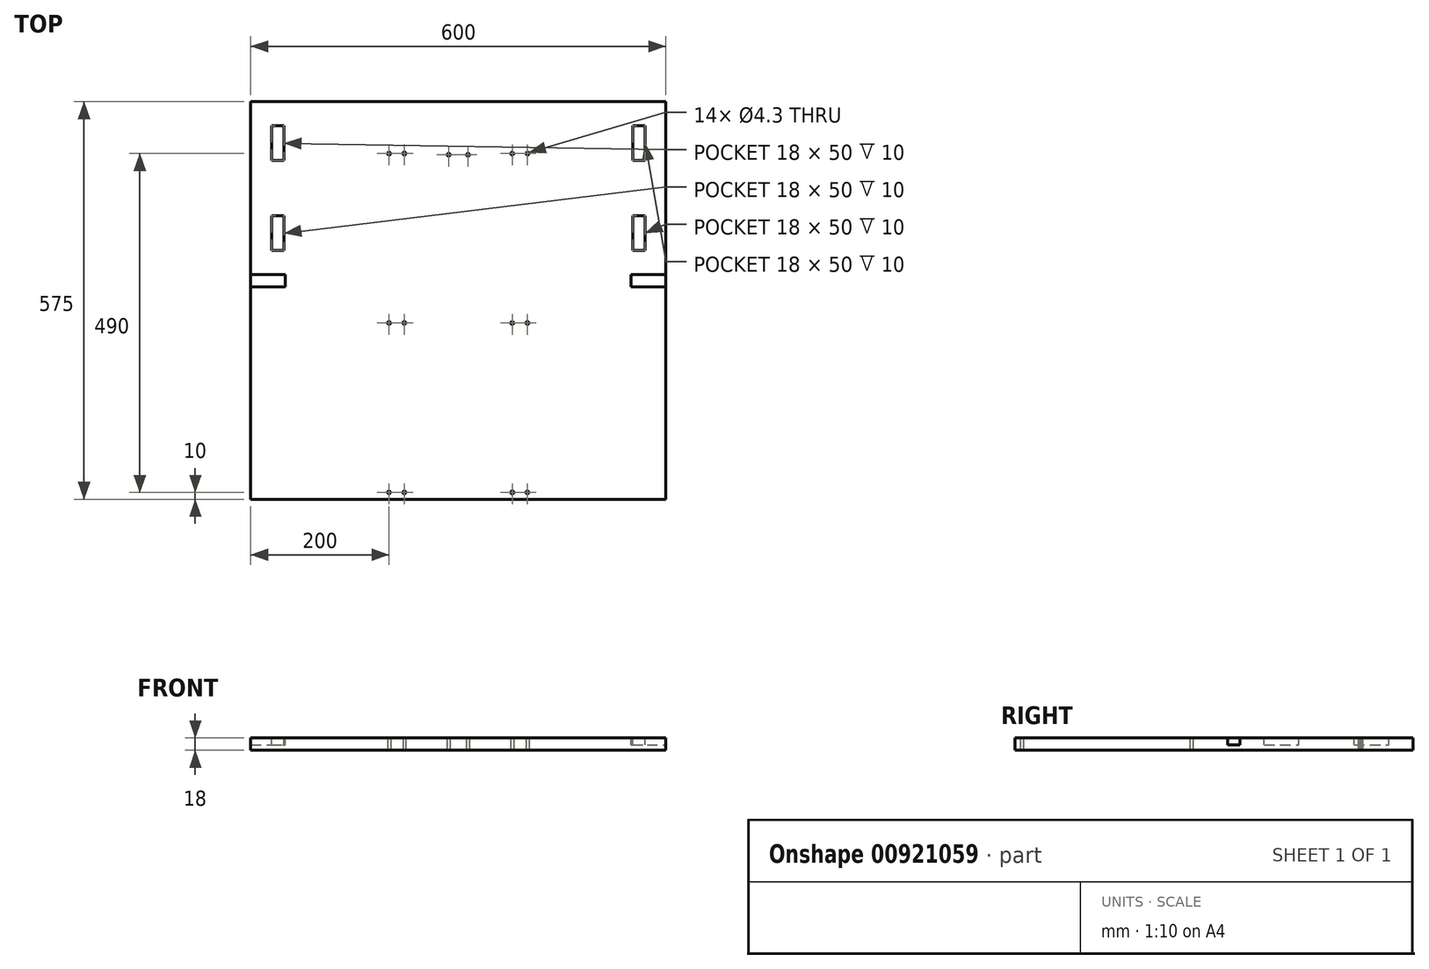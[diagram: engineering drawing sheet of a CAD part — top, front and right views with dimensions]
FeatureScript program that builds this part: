
annotation { "Feature Type Name" : "Feature", "Feature Type Description" : "" }
export const myFeature = defineFeature(function(context is Context, id is Id, definition is map)
    precondition{}
    {
        {
            var Q0;
            Q0=qCreatedBy(makeId("Top.planeOp"),FACE);
            var sketch = newSketch(context, id + "F0", { "sketchPlane" : qUnion([Q0])});
            skLineSegment(sketch, "E0.bottom", {"start": v(0, 0) * mm, "end": v(600, 0) * mm});
            skLineSegment(sketch, "E0.top", {"start": v(0, -575) * mm, "end": v(600, -575) * mm});
            skLineSegment(sketch, "E0.left", {"start": v(0, 0) * mm, "end": v(0, -575) * mm});
            skLineSegment(sketch, "E0.right", {"start": v(600, 0) * mm, "end": v(600, -575) * mm});
            skSolve(sketch);
        }
        {
            var Q0;
            Q0=makeQuery(id+"F0.imprint","IMPRINT",FACE,{"disambiguationData":[TD([[makeQuery(id+"F0.imprint","IMPRINT",EDGE,{"derivedFrom":sQuery(id+"F0.wireOp",EDGE,"E0.bottom")}),-1.0]])]});
            extrude(context, id + "F1", {"entities" : qUnion([Q0]), "depth" : 18 * mm, "offsetDistance" : 25 * mm});
        }
        {
            var Q0;
            Q0=makeQuery(id+"F1.opExtrude","CAP_FACE",FACE,{"disambiguationData":[OSD([sQuery(id+"F0.wireOp",EDGE,"E0.bottom"),sQuery(id+"F0.wireOp",EDGE,"E0.top"),sQuery(id+"F0.wireOp",EDGE,"E0.left"),sQuery(id+"F0.wireOp",EDGE,"E0.right")])],"isStart":false});
            var sketch = newSketch(context, id + "F2", { "sketchPlane" : qUnion([Q0])});
            skLineSegment(sketch, "E1.bottom", {"start": v(0, -250) * mm, "end": v(50, -250) * mm});
            skLineSegment(sketch, "E1.top", {"start": v(0, -268) * mm, "end": v(50, -268) * mm});
            skLineSegment(sketch, "E1.left", {"start": v(0, -250) * mm, "end": v(0, -268) * mm});
            skLineSegment(sketch, "E1.right", {"start": v(50, -250) * mm, "end": v(50, -268) * mm});
            skLineSegment(sketch, "E2.bottom", {"start": v(552, -215) * mm, "end": v(552, -165) * mm});
            skLineSegment(sketch, "E2.top", {"start": v(570, -215) * mm, "end": v(570, -165) * mm});
            skLineSegment(sketch, "E2.left", {"start": v(552, -215) * mm, "end": v(570, -215) * mm});
            skLineSegment(sketch, "E2.right", {"start": v(552, -165) * mm, "end": v(570, -165) * mm});
            skLineSegment(sketch, "E3.bottom", {"start": v(550, -250) * mm, "end": v(600, -250) * mm});
            skLineSegment(sketch, "E3.top", {"start": v(550, -268) * mm, "end": v(600, -268) * mm});
            skLineSegment(sketch, "E3.left", {"start": v(550, -250) * mm, "end": v(550, -268) * mm});
            skLineSegment(sketch, "E3.right", {"start": v(600, -250) * mm, "end": v(600, -268) * mm});
            skLineSegment(sketch, "E4.bottom", {"start": v(30, -85) * mm, "end": v(30, -35) * mm});
            skLineSegment(sketch, "E4.top", {"start": v(48, -85) * mm, "end": v(48, -35) * mm});
            skLineSegment(sketch, "E4.left", {"start": v(30, -85) * mm, "end": v(48, -85) * mm});
            skLineSegment(sketch, "E4.right", {"start": v(30, -35) * mm, "end": v(48, -35) * mm});
            skLineSegment(sketch, "E5.bottom", {"start": v(30, -215) * mm, "end": v(30, -165) * mm});
            skLineSegment(sketch, "E5.top", {"start": v(48, -215) * mm, "end": v(48, -165) * mm});
            skLineSegment(sketch, "E5.left", {"start": v(30, -215) * mm, "end": v(48, -215) * mm});
            skLineSegment(sketch, "E5.right", {"start": v(30, -165) * mm, "end": v(48, -165) * mm});
            skLineSegment(sketch, "E6.bottom", {"start": v(552, -85) * mm, "end": v(552, -35) * mm});
            skLineSegment(sketch, "E6.top", {"start": v(570, -85) * mm, "end": v(570, -35) * mm});
            skLineSegment(sketch, "E6.left", {"start": v(552, -85) * mm, "end": v(570, -85) * mm});
            skLineSegment(sketch, "E6.right", {"start": v(552, -35) * mm, "end": v(570, -35) * mm});
            skSolve(sketch);
        }
        {
            var Q0;
            Q0=makeQuery(id+"F2.imprint","IMPRINT",FACE,{"disambiguationData":[TD([[makeQuery(id+"F2.imprint","IMPRINT",EDGE,{"derivedFrom":sQuery(id+"F2.wireOp",EDGE,"E4.bottom")}),-1.0]])]});
            var Q1;
            Q1=makeQuery(id+"F2.imprint","IMPRINT",FACE,{"disambiguationData":[TD([[makeQuery(id+"F2.imprint","IMPRINT",EDGE,{"derivedFrom":sQuery(id+"F2.wireOp",EDGE,"E6.bottom")}),-1.0]])]});
            var Q2;
            Q2=makeQuery(id+"F2.imprint","IMPRINT",FACE,{"disambiguationData":[TD([[makeQuery(id+"F2.imprint","IMPRINT",EDGE,{"derivedFrom":sQuery(id+"F2.wireOp",EDGE,"E2.bottom")}),-1.0]])]});
            var Q3;
            Q3=makeQuery(id+"F2.imprint","IMPRINT",FACE,{"disambiguationData":[TD([[makeQuery(id+"F2.imprint","IMPRINT",EDGE,{"derivedFrom":sQuery(id+"F2.wireOp",EDGE,"E3.bottom")}),-1.0]])]});
            var Q4;
            Q4=makeQuery(id+"F2.imprint","IMPRINT",FACE,{"disambiguationData":[TD([[makeQuery(id+"F2.imprint","IMPRINT",EDGE,{"derivedFrom":sQuery(id+"F2.wireOp",EDGE,"E1.bottom")}),-1.0]])]});
            var Q5;
            Q5=makeQuery(id+"F2.imprint","IMPRINT",FACE,{"disambiguationData":[TD([[makeQuery(id+"F2.imprint","IMPRINT",EDGE,{"derivedFrom":sQuery(id+"F2.wireOp",EDGE,"E5.bottom")}),-1.0]])]});
            extrude(context, id + "F3", {"entities" : qUnion([Q0, Q1, Q2, Q3, Q4, Q5]), "operationType" : NewBodyOperationType.REMOVE, "oppositeDirection" : true, "depth" : 10 * mm, "offsetDistance" : 25 * mm});
        }
        {
            var Q0;
            Q0=makeQuery(id+"F1.opExtrude","CAP_FACE",FACE,{"disambiguationData":[OSD([sQuery(id+"F0.wireOp",EDGE,"E0.bottom"),sQuery(id+"F0.wireOp",EDGE,"E0.top"),sQuery(id+"F0.wireOp",EDGE,"E0.left"),sQuery(id+"F0.wireOp",EDGE,"E0.right")])],"isStart":false});
            var sketch = newSketch(context, id + "F4", { "sketchPlane" : qUnion([Q0])});
            skLineSegment(sketch, "E7.bottom", {"start": v(125, -197.37) * mm, "end": v(475, -197.37) * mm});
            skLineSegment(sketch, "E7.top", {"start": v(125, -432.97) * mm, "end": v(475, -432.97) * mm});
            skLineSegment(sketch, "E7.left", {"start": v(125, -197.37) * mm, "end": v(125, -432.97) * mm});
            skLineSegment(sketch, "E7.right", {"start": v(475, -197.37) * mm, "end": v(475, -432.97) * mm});
            skLineSegment(sketch, "E8", {"start": v(50, -255.93) * mm, "end": v(125, -255.93) * mm, "construction": true});
            skLineSegment(sketch, "E9", {"start": v(475, -256.27) * mm, "end": v(550, -256.27) * mm, "construction": true});
            skLineSegment(sketch, "E10.bottom", {"start": v(200, -75) * mm, "end": v(222, -75) * mm});
            skLineSegment(sketch, "E10.top", {"start": v(200, -565) * mm, "end": v(222, -565) * mm});
            skLineSegment(sketch, "E10.left", {"start": v(200, -75) * mm, "end": v(200, -565) * mm});
            skLineSegment(sketch, "E10.right", {"start": v(222, -75) * mm, "end": v(222, -565) * mm});
            skLineSegment(sketch, "E11", {"start": v(300, -197.37) * mm, "end": v(300, -432.97) * mm, "construction": true});
            skLineSegment(sketch, "E12.MirrorCS", {"start": v(400, -75) * mm, "end": v(400, -565) * mm});
            skLineSegment(sketch, "E13.MirrorCS", {"start": v(378, -75) * mm, "end": v(378, -565) * mm});
            skLineSegment(sketch, "E14.MirrorCS", {"start": v(400, -75) * mm, "end": v(378, -75) * mm});
            skLineSegment(sketch, "E15.MirrorCS", {"start": v(400, -565) * mm, "end": v(378, -565) * mm});
            skPoint(sketch, "E16", {"position": v(200, -75) * mm});
            skPoint(sketch, "E17", {"position": v(222, -75) * mm});
            skPoint(sketch, "E18", {"position": v(200, -320) * mm});
            skPoint(sketch, "E19", {"position": v(222, -320) * mm});
            skPoint(sketch, "E20", {"position": v(200, -565) * mm});
            skPoint(sketch, "E21", {"position": v(222, -565) * mm});
            skPoint(sketch, "E22", {"position": v(378, -565) * mm});
            skPoint(sketch, "E23", {"position": v(400, -565) * mm});
            skPoint(sketch, "E24", {"position": v(378, -320) * mm});
            skPoint(sketch, "E25", {"position": v(400, -320) * mm});
            skPoint(sketch, "E26", {"position": v(378, -75) * mm});
            skPoint(sketch, "E27", {"position": v(400, -75) * mm});
            skLineSegment(sketch, "E28", {"start": v(211, -565) * mm, "end": v(211, -611.84) * mm, "construction": true});
            skLineSegment(sketch, "E29", {"start": v(211, -611.84) * mm, "end": v(389, -611.84) * mm, "construction": true});
            skLineSegment(sketch, "E30", {"start": v(389, -565) * mm, "end": v(389, -611.84) * mm, "construction": true});
            skLineSegment(sketch, "E31", {"start": v(300, 0) * mm, "end": v(300, -120) * mm, "construction": true});
            skLineSegment(sketch, "E32", {"start": v(300, -120) * mm, "end": v(314, -120) * mm, "construction": true});
            skLineSegment(sketch, "E33", {"start": v(300, -120) * mm, "end": v(286, -120) * mm, "construction": true});
            skLineSegment(sketch, "E34", {"start": v(286, -120) * mm, "end": v(286, -70) * mm, "construction": true});
            skLineSegment(sketch, "E35", {"start": v(286, -70) * mm, "end": v(314, -70) * mm, "construction": true});
            skLineSegment(sketch, "E36", {"start": v(314, -70) * mm, "end": v(314, -120) * mm, "construction": true});
            skPoint(sketch, "E37", {"position": v(286, -76.76) * mm});
            skPoint(sketch, "E38", {"position": v(314, -76.76) * mm});
            skSolve(sketch);
        }
        {
            var Q0;
            Q0=sQuery(id+"F4.wireOp",VERTEX,"E16");
            var Q1;
            Q1=sQuery(id+"F4.wireOp",VERTEX,"E17");
            var Q2;
            Q2=sQuery(id+"F4.wireOp",VERTEX,"E18");
            var Q3;
            Q3=sQuery(id+"F4.wireOp",VERTEX,"E19");
            var Q4;
            Q4=sQuery(id+"F4.wireOp",VERTEX,"E26");
            var Q5;
            Q5=sQuery(id+"F4.wireOp",VERTEX,"E27");
            var Q6;
            Q6=sQuery(id+"F4.wireOp",VERTEX,"E25");
            var Q7;
            Q7=sQuery(id+"F4.wireOp",VERTEX,"E24");
            var Q8;
            Q8=sQuery(id+"F4.wireOp",VERTEX,"E22");
            var Q9;
            Q9=sQuery(id+"F4.wireOp",VERTEX,"E23");
            var Q10;
            Q10=sQuery(id+"F4.wireOp",VERTEX,"E20");
            var Q11;
            Q11=sQuery(id+"F4.wireOp",VERTEX,"E21");
            var Q12;
            Q12=makeQuery(id+"F1.opExtrude","SWEPT_BODY",BODY,{"disambiguationData":[OSD([sQuery(id+"F0.wireOp",EDGE,"E0.bottom"),sQuery(id+"F0.wireOp",EDGE,"E0.top"),sQuery(id+"F0.wireOp",EDGE,"E0.left"),sQuery(id+"F0.wireOp",EDGE,"E0.right")])]});
            hole(context, id + "F5", {"style" : HoleStyle.SIMPLE, "endStyle" : HoleEndStyle.THROUGH, "standardTappedOrClearance" : lookupTablePath({ "fit" : "Close", "standard" : "ISO", "size" : "M4", "type" : "Clearance" }), "standardBlindInLast" : lookupTablePath({ "fit" : "Close", "standard" : "ISO", "size" : "M4", "type" : "Clearance" }), "holeDiameter" : 4.3 * mm, "majorDiameter" : 5 * mm, "tappedDepth" : 12.9 * mm, "tapClearance" : 3, "locations" : qUnion([Q0, Q1, Q2, Q3, Q4, Q5, Q6, Q7, Q8, Q9, Q10, Q11]), "scope" : qUnion([Q12])});
        }
        {
            var Q0;
            Q0=sQuery(id+"F4.wireOp",VERTEX,"E37");
            var Q1;
            Q1=sQuery(id+"F4.wireOp",VERTEX,"E38");
            var Q2;
            Q2=makeQuery(id+"F1.opExtrude","SWEPT_BODY",BODY,{"disambiguationData":[OSD([sQuery(id+"F0.wireOp",EDGE,"E0.bottom"),sQuery(id+"F0.wireOp",EDGE,"E0.top"),sQuery(id+"F0.wireOp",EDGE,"E0.left"),sQuery(id+"F0.wireOp",EDGE,"E0.right")])]});
            hole(context, id + "F6", {"style" : HoleStyle.SIMPLE, "endStyle" : HoleEndStyle.THROUGH, "standardTappedOrClearance" : lookupTablePath({ "fit" : "Close", "standard" : "ISO", "size" : "M4", "type" : "Clearance" }), "standardBlindInLast" : lookupTablePath({ "fit" : "Close", "standard" : "ISO", "size" : "M4", "type" : "Clearance" }), "holeDiameter" : 4.3 * mm, "majorDiameter" : 5 * mm, "tappedDepth" : 12.9 * mm, "tapClearance" : 3, "locations" : qUnion([Q0, Q1]), "scope" : qUnion([Q2])});
        }
    });
